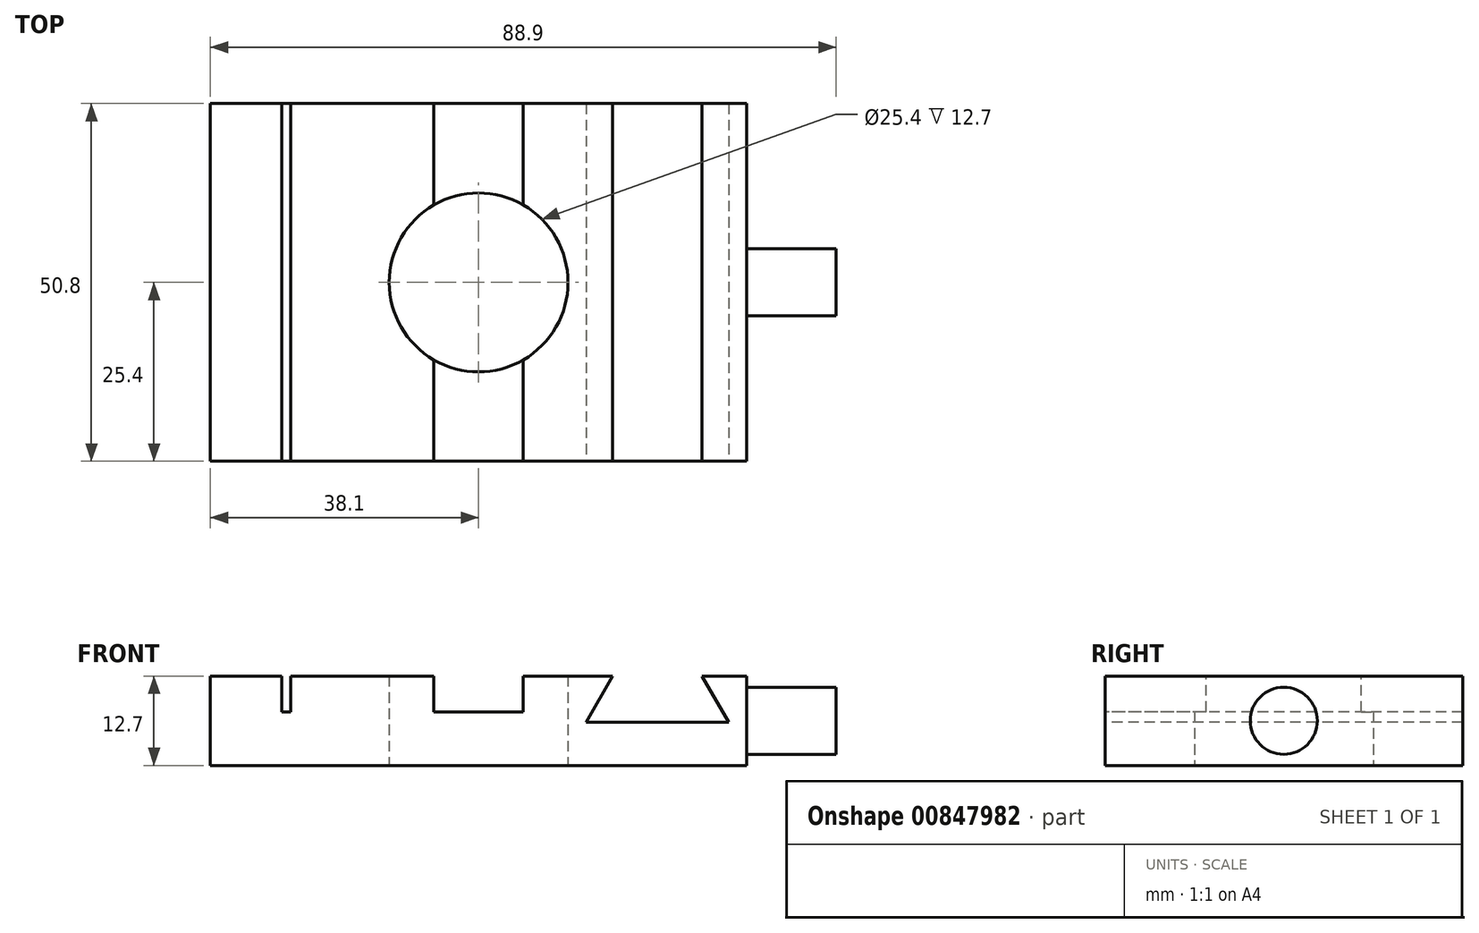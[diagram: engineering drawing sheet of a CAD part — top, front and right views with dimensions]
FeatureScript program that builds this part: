
annotation { "Feature Type Name" : "Feature", "Feature Type Description" : "" }
export const myFeature = defineFeature(function(context is Context, id is Id, definition is map)
    precondition{}
    {
        {
            var Q0;
            Q0=qCreatedBy(makeId("Top.planeOp"),FACE);
            var sketch = newSketch(context, id + "F0", { "sketchPlane" : qUnion([Q0])});
            skLineSegment(sketch, "E0.bottom", {"start": v(38.1, 25.4) * mm, "end": v(-38.1, 25.4) * mm});
            skLineSegment(sketch, "E0.top", {"start": v(38.1, -25.4) * mm, "end": v(-38.1, -25.4) * mm});
            skLineSegment(sketch, "E0.left", {"start": v(38.1, 25.4) * mm, "end": v(38.1, -25.4) * mm});
            skLineSegment(sketch, "E0.right", {"start": v(-38.1, 25.4) * mm, "end": v(-38.1, -25.4) * mm});
            skPoint(sketch, "E0.middle", {"position": v(0, 0) * mm});
            skCircle(sketch, "E1", {"center": v(0, 0) * mm, "radius": 12.7 * mm});
            skSolve(sketch);
        }
        {
            var Q0;
            Q0=makeQuery(id+"F0.imprint","IMPRINT",FACE,{"disambiguationData":[TD([[makeQuery(id+"F0.imprint","IMPRINT",EDGE,{"derivedFrom":sQuery(id+"F0.wireOp",EDGE,"E0.bottom")}),1.0]])]});
            extrude(context, id + "F1", {"entities" : qUnion([Q0]), "depth" : 12.7 * mm, "offsetDistance" : 25.4 * mm});
        }
        {
            var Q0;
            Q0=makeQuery(id+"F1.opExtrude","CAP_FACE",FACE,{"disambiguationData":[OSD([sQuery(id+"F0.wireOp",EDGE,"E0.bottom"),sQuery(id+"F0.wireOp",EDGE,"E0.top"),sQuery(id+"F0.wireOp",EDGE,"E0.left"),sQuery(id+"F0.wireOp",EDGE,"E0.right"),sQuery(id+"F0.wireOp",EDGE,"E1")])],"isStart":false});
            var sketch = newSketch(context, id + "F2", { "sketchPlane" : qUnion([Q0])});
            skLineSegment(sketch, "E2.bottom", {"start": v(-27.94, 25.4) * mm, "end": v(-26.67, 25.4) * mm});
            skLineSegment(sketch, "E2.top", {"start": v(-27.94, -25.4) * mm, "end": v(-26.67, -25.4) * mm});
            skLineSegment(sketch, "E2.left", {"start": v(-27.94, 25.4) * mm, "end": v(-27.94, -25.4) * mm});
            skLineSegment(sketch, "E2.right", {"start": v(-26.67, 25.4) * mm, "end": v(-26.67, -25.4) * mm});
            skLineSegment(sketch, "E3", {"start": v(-6.35, 25.4) * mm, "end": v(-6.35, -25.4) * mm});
            skLineSegment(sketch, "E4", {"start": v(-6.35, -25.4) * mm, "end": v(6.35, -25.4) * mm});
            skLineSegment(sketch, "E5", {"start": v(6.35, -25.4) * mm, "end": v(6.35, 25.4) * mm});
            skLineSegment(sketch, "E6", {"start": v(6.35, 25.4) * mm, "end": v(-6.35, 25.4) * mm, "construction": true});
            skPoint(sketch, "E7", {"position": v(0, 0) * mm});
            skPoint(sketch, "E8", {"position": v(0, -25.4) * mm});
            skLineSegment(sketch, "E9", {"start": v(0, 25.4) * mm, "end": v(0, -25.4) * mm, "construction": true});
            skSolve(sketch);
        }
        {
            var Q0;
            Q0=makeQuery(id+"F2.imprint","IMPRINT",FACE,{"disambiguationData":[TD([[makeQuery(id+"F2.imprint","IMPRINT",EDGE,{"derivedFrom":sQuery(id+"F2.wireOp",EDGE,"E2.bottom")}),1.0]])]});
            var Q1;
            {var subQ0=sQuery(id+"F2.wireOp",EDGE,"E3");var subQ1=makeQuery(id+"F1.opExtrude","CAP_EDGE",EDGE,{"disambiguationData":[OSD([sQuery(id+"F0.wireOp",EDGE,"E0.bottom")])],"isStart":false});var subQ2=makeQuery(id+"F2.imprint","INTERSECT",VERTEX,{"derivedFrom":[subQ1,subQ0]});Q1=makeQuery(id+"F2.imprint","IMPRINT",FACE,{"disambiguationData":[TD([[makeQuery(id+"F2.imprint","IMPRINT",EDGE,{"disambiguationData":[TD([[subQ2,-1.0]])],"derivedFrom":subQ0}),1.0]])]});}
            var Q2;
            {var subQ0=sQuery(id+"F2.wireOp",EDGE,"E4");Q2=makeQuery(id+"F2.imprint","IMPRINT",FACE,{"disambiguationData":[TD([[makeQuery(id+"F2.imprint","IMPRINT",EDGE,{"derivedFrom":subQ0}),-1.0]])]});}
            extrude(context, id + "F3", {"entities" : qUnion([Q0, Q1, Q2]), "operationType" : NewBodyOperationType.REMOVE, "oppositeDirection" : true, "depth" : 5.08 * mm, "offsetDistance" : 25.4 * mm});
        }
        {
            var Q0;
            Q0=makeQuery(id+"F1.opExtrude","SWEPT_FACE",FACE,{"disambiguationData":[OSD([sQuery(id+"F0.wireOp",EDGE,"E0.top")])]});
            var sketch = newSketch(context, id + "F4", { "sketchPlane" : qUnion([Q0])});
            skLineSegment(sketch, "E10", {"start": v(19.05, 12.7) * mm, "end": v(15.27, 6.16) * mm});
            skLineSegment(sketch, "E11", {"start": v(15.27, 6.16) * mm, "end": v(35.53, 6.16) * mm});
            skLineSegment(sketch, "E12", {"start": v(35.53, 6.16) * mm, "end": v(31.75, 12.7) * mm});
            skLineSegment(sketch, "E13", {"start": v(25.4, 6.16) * mm, "end": v(25.4, 12.7) * mm, "construction": true});
            skPoint(sketch, "E13.endSnap0", {"position": v(22.23, 12.7) * mm});
            skSolve(sketch);
        }
        {
            var Q0;
            Q0 = qSketchRegion(id + "F4", true);
            var Q1;
            {var subQ0=sQuery(id+"F4.wireOp",EDGE,"E10");Q1=makeQuery(id+"F4.imprint","IMPRINT",FACE,{"disambiguationData":[TD([[makeQuery(id+"F4.imprint","IMPRINT",EDGE,{"derivedFrom":subQ0}),1.0]])]});}
            extrude(context, id + "F5", {"entities" : qUnion([Q0, Q1]), "operationType" : NewBodyOperationType.REMOVE, "endBound" : BoundingType.THROUGH_ALL, "oppositeDirection" : true, "depth" : 50.55 * mm, "offsetDistance" : 25.4 * mm});
        }
        {
            var Q0;
            Q0=makeQuery(id+"F1.opExtrude","SWEPT_FACE",FACE,{"disambiguationData":[OSD([sQuery(id+"F0.wireOp",EDGE,"E0.left")])]});
            var sketch = newSketch(context, id + "F6", { "sketchPlane" : qUnion([Q0])});
            skCircle(sketch, "E14", {"center": v(0, 6.35) * mm, "radius": 4.76 * mm});
            skPoint(sketch, "E14.centerSnap0", {"position": v(-25.4, 6.35) * mm});
            skPoint(sketch, "E14.centerSnap1", {"position": v(0, 12.7) * mm});
            skSolve(sketch);
        }
        {
            var Q0;
            Q0=makeQuery(id+"F6.imprint","IMPRINT",FACE,{"disambiguationData":[TD([[makeQuery(id+"F6.imprint","IMPRINT",EDGE,{"derivedFrom":sQuery(id+"F6.wireOp",EDGE,"E14")}),1.0]])]});
            extrude(context, id + "F7", {"entities" : qUnion([Q0]), "operationType" : NewBodyOperationType.ADD, "depth" : 12.7 * mm, "offsetDistance" : 25.4 * mm});
        }
    });
